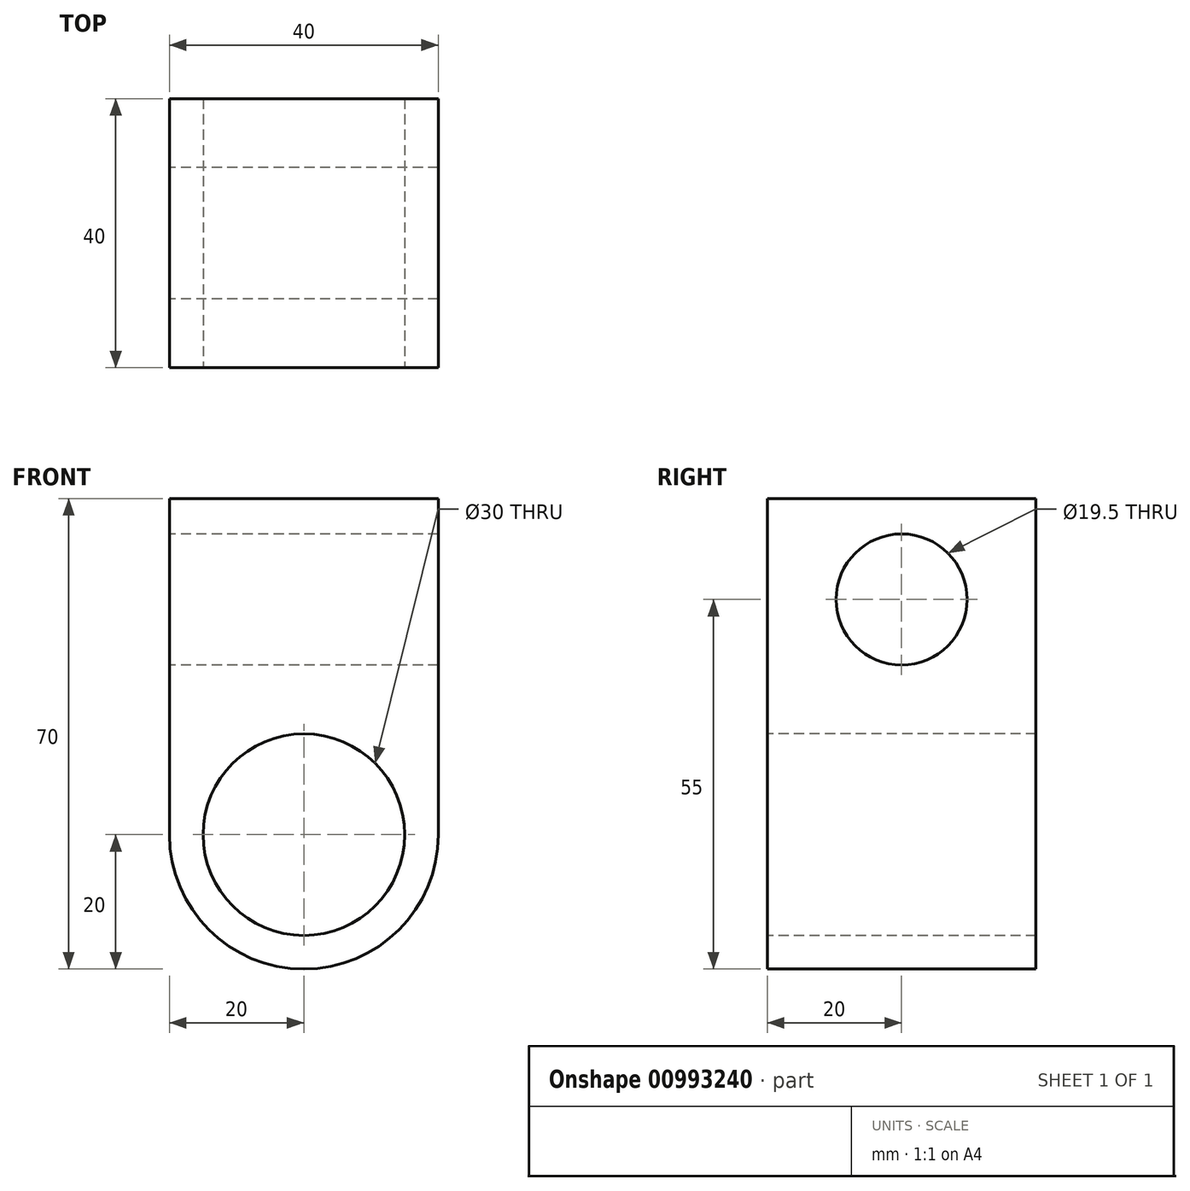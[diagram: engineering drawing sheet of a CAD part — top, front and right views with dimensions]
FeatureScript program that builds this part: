
annotation { "Feature Type Name" : "Feature", "Feature Type Description" : "" }
export const myFeature = defineFeature(function(context is Context, id is Id, definition is map)
    precondition{}
    {
        {
            var Q0;
            Q0=qCreatedBy(makeId("Front.planeOp"),FACE);
            var sketch = newSketch(context, id + "F0", { "sketchPlane" : qUnion([Q0])});
            skLineSegment(sketch, "E0.bottom", {"start": v(-20, 35) * mm, "end": v(20, 35) * mm});
            skLineSegment(sketch, "E0.top", {"start": v(-20, -35) * mm, "end": v(20, -35) * mm});
            skLineSegment(sketch, "E0.left", {"start": v(-20, 35) * mm, "end": v(-20, -35) * mm});
            skLineSegment(sketch, "E0.right", {"start": v(20, 35) * mm, "end": v(20, -35) * mm});
            skSolve(sketch);
        }
        {
            var Q0;
            Q0 = qSketchRegion(id + "F0", true);
            extrude(context, id + "F1", {"entities" : qUnion([Q0]), "depth" : 20 * mm, "offsetDistance" : 25 * mm, "hasSecondDirection" : true, "secondDirectionOppositeDirection" : true, "secondDirectionDepth" : 20 * mm});
        }
        {
            var Q0;
            Q0=makeQuery(id+"F1.opExtrude","SWEPT_FACE",FACE,{"disambiguationData":[OSD([sQuery(id+"F0.wireOp",EDGE,"E0.left")])]});
            var sketch = newSketch(context, id + "F2", { "sketchPlane" : qUnion([Q0])});
            skPoint(sketch, "E1", {"position": v(0, 20) * mm});
            skSolve(sketch);
        }
        {
            var Q0;
            Q0=sQuery(id+"F2.wireOp",VERTEX,"E1");
            var Q1;
            Q1=makeQuery(id+"F1.opExtrude","SWEPT_BODY",BODY,{"disambiguationData":[OSD([sQuery(id+"F0.wireOp",EDGE,"E0.bottom"),sQuery(id+"F0.wireOp",EDGE,"E0.top"),sQuery(id+"F0.wireOp",EDGE,"E0.left"),sQuery(id+"F0.wireOp",EDGE,"E0.right")])]});
            hole(context, id + "F3", {"style" : HoleStyle.SIMPLE, "endStyle" : HoleEndStyle.THROUGH, "holeDiameter" : 19.5 * mm, "majorDiameter" : 5 * mm, "isTappedThrough" : true, "tappedDepth" : 12 * mm, "tapClearance" : 3, "locations" : qUnion([Q0]), "scope" : qUnion([Q1])});
        }
        {
            var Q0;
            Q0=makeQuery(id+"F1.opExtrude","CAP_FACE",FACE,{"disambiguationData":[OSD([sQuery(id+"F0.wireOp",EDGE,"E0.bottom"),sQuery(id+"F0.wireOp",EDGE,"E0.top"),sQuery(id+"F0.wireOp",EDGE,"E0.left"),sQuery(id+"F0.wireOp",EDGE,"E0.right")])],"isStart":false});
            var sketch = newSketch(context, id + "F4", { "sketchPlane" : qUnion([Q0])});
            skPoint(sketch, "E2", {"position": v(0, -15) * mm});
            skSolve(sketch);
        }
        {
            var Q0;
            Q0=sQuery(id+"F4.wireOp",VERTEX,"E2");
            var Q1;
            Q1=makeQuery(id+"F1.opExtrude","SWEPT_BODY",BODY,{"disambiguationData":[OSD([sQuery(id+"F0.wireOp",EDGE,"E0.bottom"),sQuery(id+"F0.wireOp",EDGE,"E0.top"),sQuery(id+"F0.wireOp",EDGE,"E0.left"),sQuery(id+"F0.wireOp",EDGE,"E0.right")])]});
            hole(context, id + "F5", {"style" : HoleStyle.SIMPLE, "endStyle" : HoleEndStyle.THROUGH, "holeDiameter" : 30 * mm, "majorDiameter" : 5 * mm, "isTappedThrough" : true, "tappedDepth" : 12 * mm, "tapClearance" : 3, "locations" : qUnion([Q0]), "scope" : qUnion([Q1])});
        }
        {
            var Q0;
            Q0=makeQuery(id+"F1.opExtrude","SWEPT_EDGE",EDGE,{"disambiguationData":[OSD([sQuery(id+"F0.wireOp",EDGE,"E0.top"),sQuery(id+"F0.wireOp",EDGE,"E0.right")])]});
            var Q1;
            Q1=makeQuery(id+"F1.opExtrude","SWEPT_EDGE",EDGE,{"disambiguationData":[OSD([sQuery(id+"F0.wireOp",EDGE,"E0.top"),sQuery(id+"F0.wireOp",EDGE,"E0.left")])]});
            fillet(context, id + "F6", {"entities" : qUnion([Q0, Q1]), "radius" : 20 * mm, "tangentPropagation" : true, "allowEdgeOverflow" : false});
        }
    });
